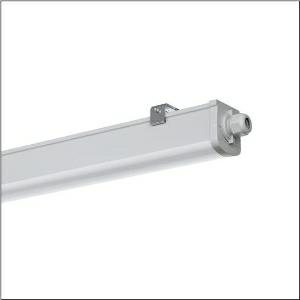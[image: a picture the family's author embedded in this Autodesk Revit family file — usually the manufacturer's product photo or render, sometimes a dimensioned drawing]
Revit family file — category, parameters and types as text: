
# Revit family: monsun_r__31_51fa207k450b_1d2e
name_source: partatom
category: Lighting Fixtures
units: mm (PartAtom-declared; Revit-internal decimal feet)

## family parameters
Cut with Voids When Loaded = No
Host = Face
Light Source = No
Part Type = Normal
Room Calculation Point = No
Round Connector Dimension = Use Diameter
Shared = No

## types (1)
- Monsun® 31 (1 x LED, 5100 lm, 38 W, 4000K)
    Apparent Load = 38 VA
    CIE Flux Codes = 42 72 91 92 100
    Color Rendering = 80
    Color Temperature = 4000K
    Default Elevation = 1800 mm
    Description = Monsun® 31, damp-proof luminaire, primary optical cover: diffuser, of PC, frosted, light emission: direct distribution, primary light characteristic: symmetric, installation type: surface-mounted, LED, rated luminous flux: 5.100lm, luminous efficacy: 134lm/W, light colour: 840, colour temperature: 4000K, control gear: ON/OFF, with terminal, 3+1-pole, max. 2.5mm², through-wiring: 3x 2.5mm² + 1x 1.5mm², mains connection: 220..240V, AC, 50/60Hz, rated input power: 38W, housing, luminaire housing, of PC, light grey (RAL 7035), length: 1.158mm, width: 68mm, height: 76mm, protection rating (complete): IP66, insulation class (complete): insulation class II (safety insulation), certification: CE, ENEC, UKCA, protection symbol: D, impact resistance: IK08, permissible operating ambient temperature: -20..+40°C, corresponds to IFS (International Featured Standards) requirements for safety and quality in the food industry, contact your sales advisor before using the luminaires in applications with unclear chemical exposure, large temperature fluctuations or condensation-forming humidity, packaging unit: 1 piece
    Height = 77 mm
    Lamp = 1 x LED
    Lamp Light Flux = 5100 lm
    Lamp Power = 38 W
    Lamp count = 1
    Length = 1218 mm
    Luminous efficacy = 134 lm/W
    Manufacturer = Siteco
    ModVariant = No
    Model = 51FA207K450B
    Mounting Place = Ceiling
    Mounting Type = Surface mounted
    Number of Poles = 1
    OnlyDefault = Yes
    Power Factor = 1
    Product Name = Monsun® 31
    Product group = damp-proof luminaire
    ProductGroupID = 300
    Protection Class = Protection class II
    Protection Degree = IP 66
    RLX_Detail_Level = 1
    RLX_Emergency_Light_Flux = 0 lm
    RLX_Emergency_Type = 0
    RLX_Emergency_Type_DB = No
    RlxData = <blob elided: 33009 chars, md5=982bb4f3>
    Socket = socket
    Standby Power = 0 W
    System Light Flux = 5100 lm
    System Power = 38 W
    Type Comments = Product without accessories
    Type Image = l_1006174.jpg
    URL = http://relux.com
    VarID = ---
    Voltage = 0 V
    Weight = 0.00 kg
    Width = 69 mm

## geometry (parser evidence)
native form markers: Blend x4, Sweep x14
no freeform markers — native parametric forms only
